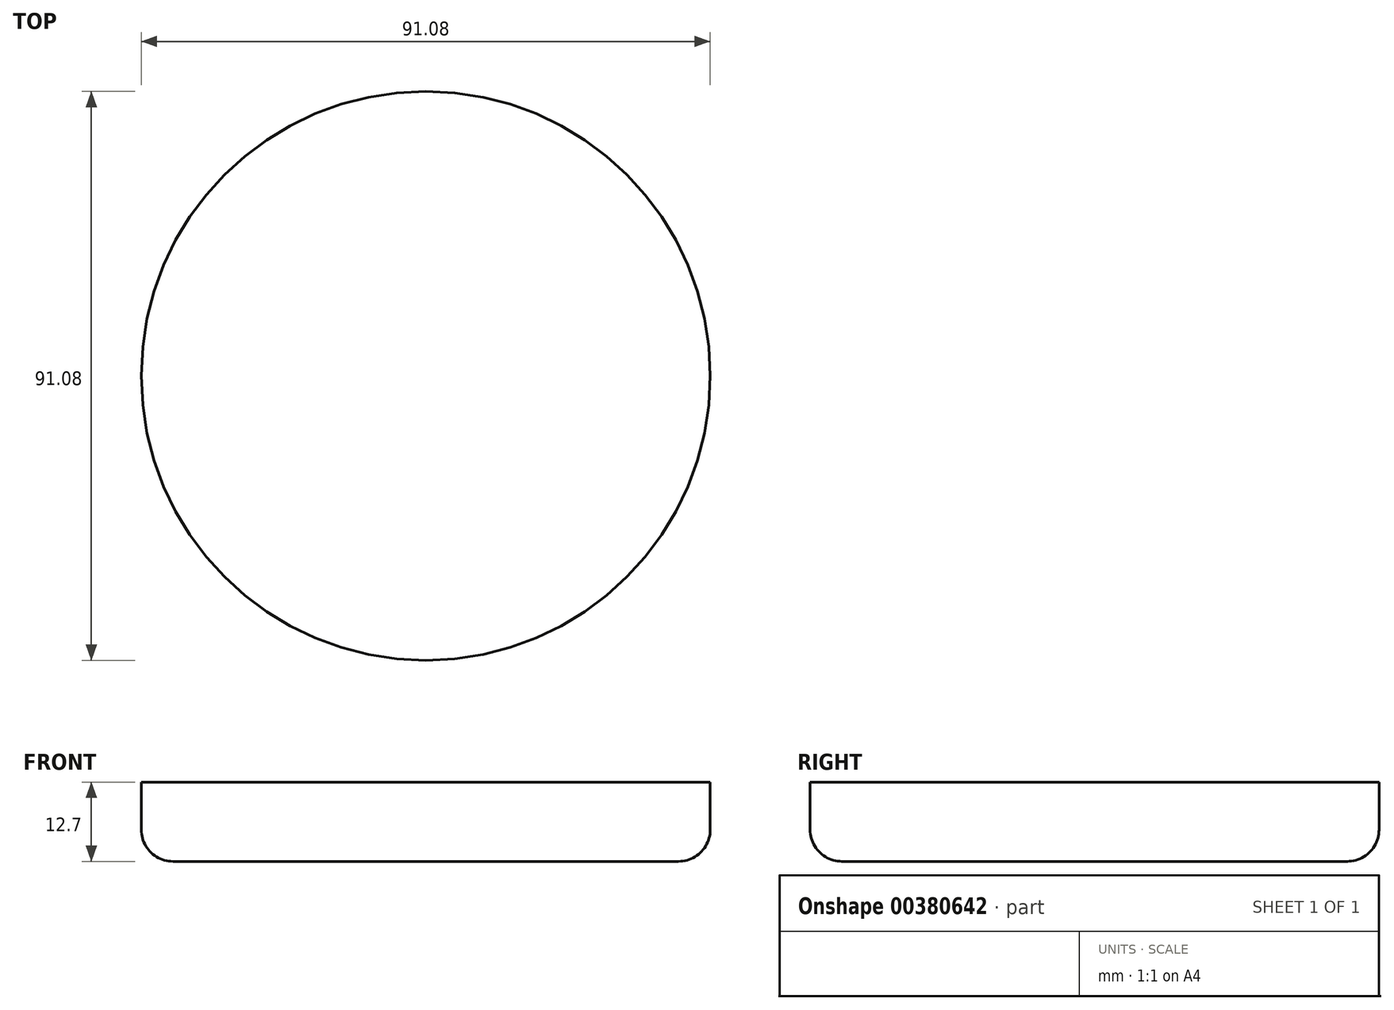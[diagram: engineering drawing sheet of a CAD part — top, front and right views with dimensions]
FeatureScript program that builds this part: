
annotation { "Feature Type Name" : "Feature", "Feature Type Description" : "" }
export const myFeature = defineFeature(function(context is Context, id is Id, definition is map)
    precondition{}
    {
        {
            var Q0;
            Q0=qCreatedBy(makeId("Top.planeOp"),FACE);
            var sketch = newSketch(context, id + "F0", { "sketchPlane" : qUnion([Q0])});
            skCircle(sketch, "E0", {"center": v(0, 0) * mm, "radius": 45.54 * mm});
            skSolve(sketch);
        }
        {
            var Q0;
            Q0=makeQuery(id+"F0.imprint","IMPRINT",FACE,{"disambiguationData":[TD([[makeQuery(id+"F0.imprint","IMPRINT",EDGE,{"derivedFrom":sQuery(id+"F0.wireOp",EDGE,"E0")}),1.0]])]});
            var Q1;
            Q1=sQuery(id+"F0.wireOp",EDGE,"E0");
            extrude(context, id + "F1", {"entities" : qUnion([Q0]), "surfaceEntities" : qUnion([Q1]), "oppositeDirection" : true, "depth" : 12.7 * mm});
        }
        {
            var Q0;
            Q0=makeQuery(id+"F1.opExtrude","CAP_EDGE",EDGE,{"disambiguationData":[OSD([sQuery(id+"F0.wireOp",EDGE,"E0")])],"isStart":false});
            fillet(context, id + "F2", {"entities" : qUnion([Q0]), "radius" : 5.08 * mm, "tangentPropagation" : true, "allowEdgeOverflow" : false});
        }
    });
